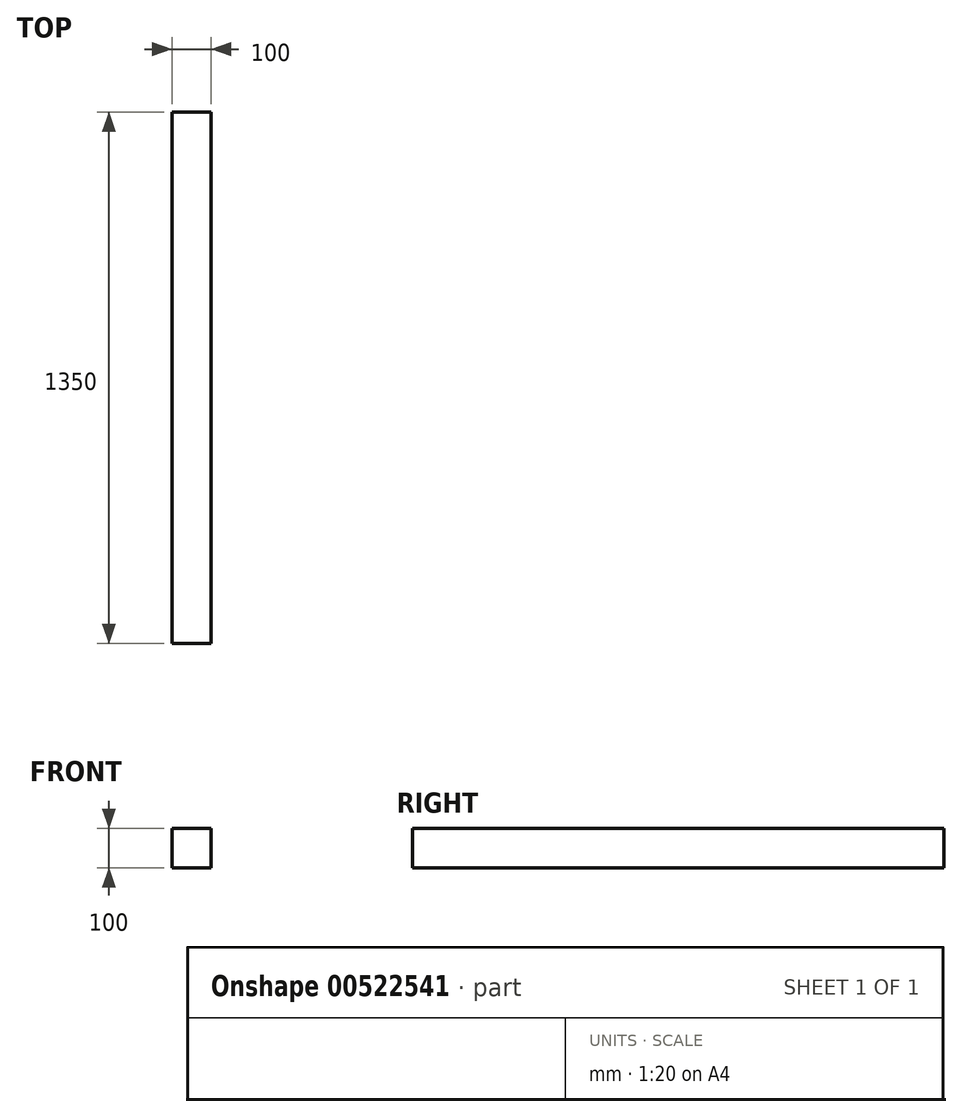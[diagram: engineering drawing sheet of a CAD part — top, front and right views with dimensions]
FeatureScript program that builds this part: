
annotation { "Feature Type Name" : "Feature", "Feature Type Description" : "" }
export const myFeature = defineFeature(function(context is Context, id is Id, definition is map)
    precondition{}
    {
        {
            var Q0;
            Q0=qCreatedBy(makeId("Front.planeOp"),FACE);
            var sketch = newSketch(context, id + "F0", { "sketchPlane" : qUnion([Q0])});
            skLineSegment(sketch, "E0.bottom", {"start": v(-118.75, 94.8) * mm, "end": v(-18.75, 94.8) * mm});
            skLineSegment(sketch, "E0.top", {"start": v(-118.75, -5.2) * mm, "end": v(-18.75, -5.2) * mm});
            skLineSegment(sketch, "E0.left", {"start": v(-118.75, 94.8) * mm, "end": v(-118.75, -5.2) * mm});
            skLineSegment(sketch, "E0.right", {"start": v(-18.75, 94.8) * mm, "end": v(-18.75, -5.2) * mm});
            skSolve(sketch);
        }
        {
            var Q0;
            Q0=qSketchRegion(id+"F0",true);
            extrude(context, id + "F1", {"entities" : qUnion([Q0]), "depth" : 1350 * mm, "offsetDistance" : 25 * mm});
        }
    });
